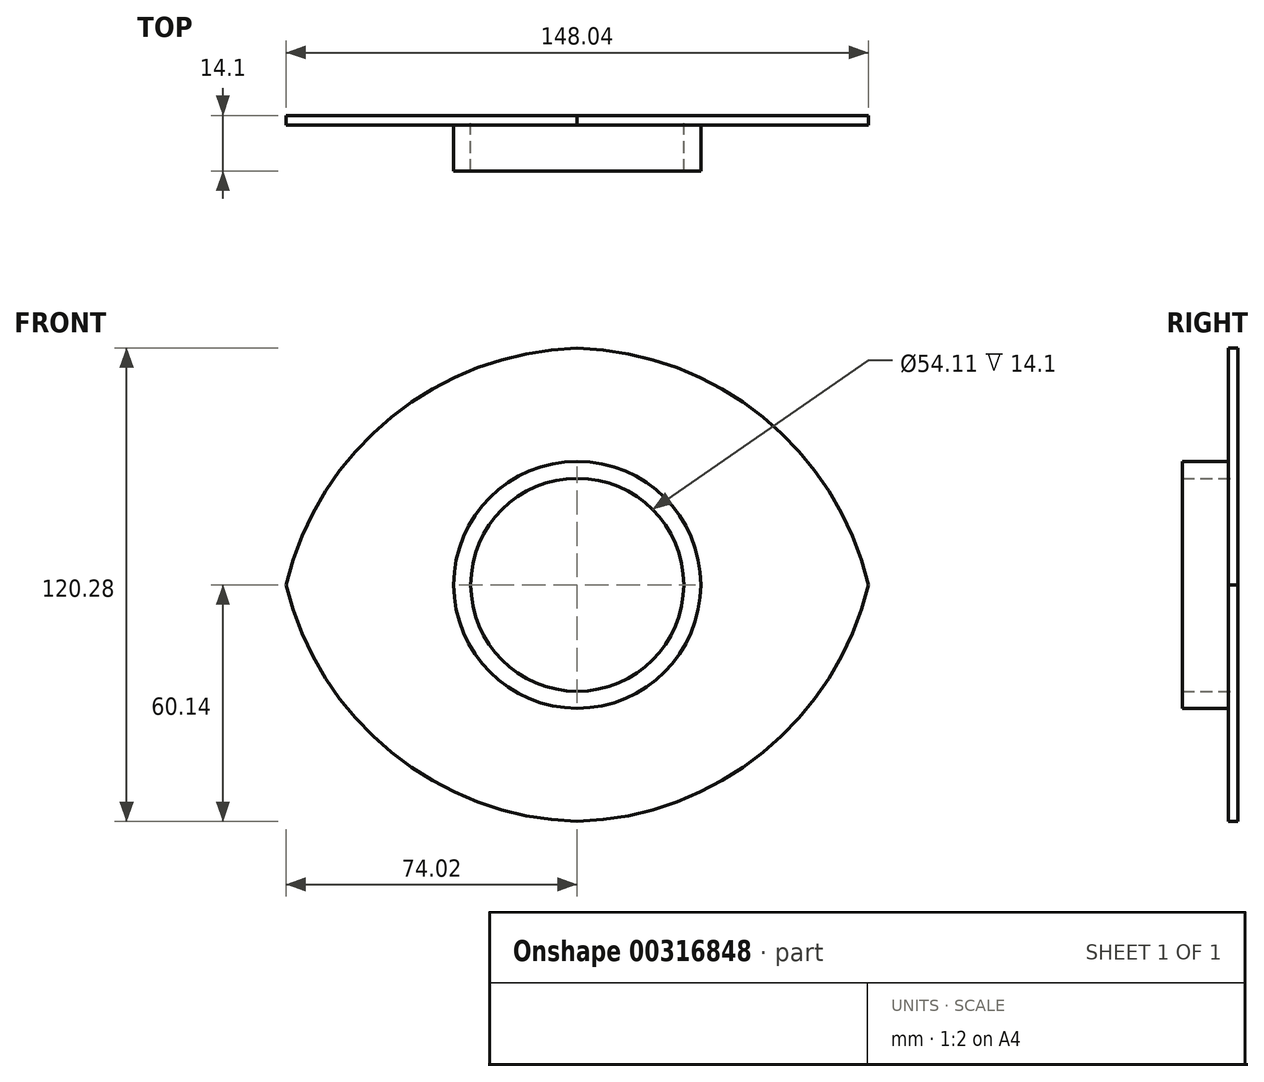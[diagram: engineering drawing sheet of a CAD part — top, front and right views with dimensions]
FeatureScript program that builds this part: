
annotation { "Feature Type Name" : "Feature", "Feature Type Description" : "" }
export const myFeature = defineFeature(function(context is Context, id is Id, definition is map)
    precondition{}
    {
        {
            var Q0;
            Q0=qCreatedBy(makeId("Front.planeOp"),FACE);
            var sketch = newSketch(context, id + "F0", { "sketchPlane" : qUnion([Q0])});
            skLineSegment(sketch, "E0.bottom", {"start": v(-76.18, 60.17) * mm, "end": v(76.18, 60.17) * mm});
            skLineSegment(sketch, "E0.left", {"start": v(-76.18, 60.17) * mm, "end": v(-76.18, -34.16) * mm});
            skLineSegment(sketch, "E1.MirrorCS", {"start": v(76.18, 60.17) * mm, "end": v(-76.18, 60.17) * mm});
            skLineSegment(sketch, "E2.MirrorCS", {"start": v(76.18, 60.17) * mm, "end": v(76.18, -34.16) * mm});
            skLineSegment(sketch, "E3.MirrorCS", {"start": v(76.18, -60.17) * mm, "end": v(-76.18, -60.17) * mm});
            skLineSegment(sketch, "E4.MirrorCS", {"start": v(76.18, -60.17) * mm, "end": v(76.18, 34.16) * mm});
            skLineSegment(sketch, "E5.MirrorCS", {"start": v(-76.18, -60.17) * mm, "end": v(-76.18, 34.16) * mm});
            skPoint(sketch, "E0.top.end.orphan", {"position": v(76.18, -34.16) * mm});
            skCircle(sketch, "E6", {"center": v(0, 0) * mm, "radius": 31.37 * mm});
            skCircle(sketch, "E7", {"center": v(0, 0) * mm, "radius": 27.05 * mm});
            skSolve(sketch);
        }
        {
            var Q0;
            {var subQ2=sQuery(id+"F0.wireOp",EDGE,"E0.left");Q0=makeQuery(id+"F0.imprint","IMPRINT",FACE,{"disambiguationData":[TD([[makeQuery(id+"F0.imprint","IMPRINT",EDGE,{"derivedFrom":subQ2}),1.0]])]});}
            extrude(context, id + "F1", {"entities" : qUnion([Q0]), "depth" : 2.4 * mm});
        }
        {
            var Q0;
            Q0=makeQuery(id+"F0.imprint","IMPRINT",FACE,{"disambiguationData":[TD([[makeQuery(id+"F0.imprint","IMPRINT",EDGE,{"derivedFrom":sQuery(id+"F0.wireOp",EDGE,"E6")}),1.0]])]});
            extrude(context, id + "F2", {"entities" : qUnion([Q0]), "operationType" : NewBodyOperationType.ADD, "depth" : 14.1 * mm});
        }
        {
            var Q0;
            Q0=makeQuery(id+"F1.opExtrude","SWEPT_EDGE",EDGE,{"disambiguationData":[OSD([sQuery(id+"F0.wireOp",EDGE,"E0.left"),sQuery(id+"F0.wireOp",EDGE,"E1.MirrorCS")])]});
            var Q1;
            Q1=makeQuery(id+"F1.opExtrude","SWEPT_EDGE",EDGE,{"disambiguationData":[OSD([sQuery(id+"F0.wireOp",EDGE,"E1.MirrorCS"),sQuery(id+"F0.wireOp",EDGE,"E2.MirrorCS")])]});
            var Q2;
            Q2=makeQuery(id+"F1.opExtrude","SWEPT_EDGE",EDGE,{"disambiguationData":[OSD([sQuery(id+"F0.wireOp",EDGE,"E3.MirrorCS"),sQuery(id+"F0.wireOp",EDGE,"E4.MirrorCS")])]});
            var Q3;
            Q3=makeQuery(id+"F1.opExtrude","SWEPT_EDGE",EDGE,{"disambiguationData":[OSD([sQuery(id+"F0.wireOp",EDGE,"E3.MirrorCS"),sQuery(id+"F0.wireOp",EDGE,"E5.MirrorCS")])]});
            fillet(context, id + "F3", {"entities" : qUnion([Q0, Q1, Q2, Q3]), "radius" : 78.46 * mm, "tangentPropagation" : true, "allowEdgeOverflow" : false});
        }
    });
